# Revit family: Furniture_Shelving-Storage_KUMI_Kladskap
name_source: partatom
category: Furniture
revit_build: Autodesk Revit 2018 (Build: 20190510_1515(x64)
units: mm (PartAtom-declared; Revit-internal decimal feet)

## family parameters
Always vertical = No
Cut with Voids When Loaded = No
OmniClass Number = 23.21.15.11
OmniClass Title = Wardrobes
Room Calculation Point = No
Shared = No
Work Plane-Based = Yes

## types (1)
- Furniture_Shelving-Storage_KUMI_Kladskap
    BIMobject category = Shelving & Storage
    Default Elevation = 1219.2 mm  [stored 4 ft]
    Description = Fully welded and powder-coated wardrobe made of sheet steel. The paintwork provides a durable surface, which means that the wardrobe is particularly suitable in public environments such as gyms, bathhouses, sports facilities, offices and changing rooms at workplaces. Each cabinet is equipped with a hat shelf, clothes rail, two removable hooks and a padlock latch. The doors are recessed in the front frame with hidden hinges. The wardrobe is ventilated by drafts at the top and bottom.
    Design country = Sweden
    Edition number = 1
    Handle Material = Kumi - Steel - Metal
    Manufacturer = KUMI
    Manufacturer name = KUMI
    Material main = Steel
    Model = Wardrobe 3 Doors Width 900 mm - 13111002
    Product Guid = f29f630a-e6e8-44e9-a0b2-7f14f6c54960
    Product SKU = kumi-wardrobe
    Product data url = https://bimobject.com
    Product family = Wardrobe
    Product group = Cabinets
    Product name = Klädskåp
    Product url = https://www.kumi.se
    QR code = https://bimobject.com
    Type - (Wardrobe 2 Doors Width 600 mm) = Yes
    Type - (Wardrobe 3 Doors Width 900 mm) = No
    Type - (Wardrobe 4 Doors Width 1200 mm) = No
    URL = https://www.kumi.se

note: [stored X ft] marks values corroborated as IEEE doubles in the binary element streams (Revit-internal decimal feet)

## geometry (parser evidence)
native form markers: Sweep x3
no freeform markers — native parametric forms only
